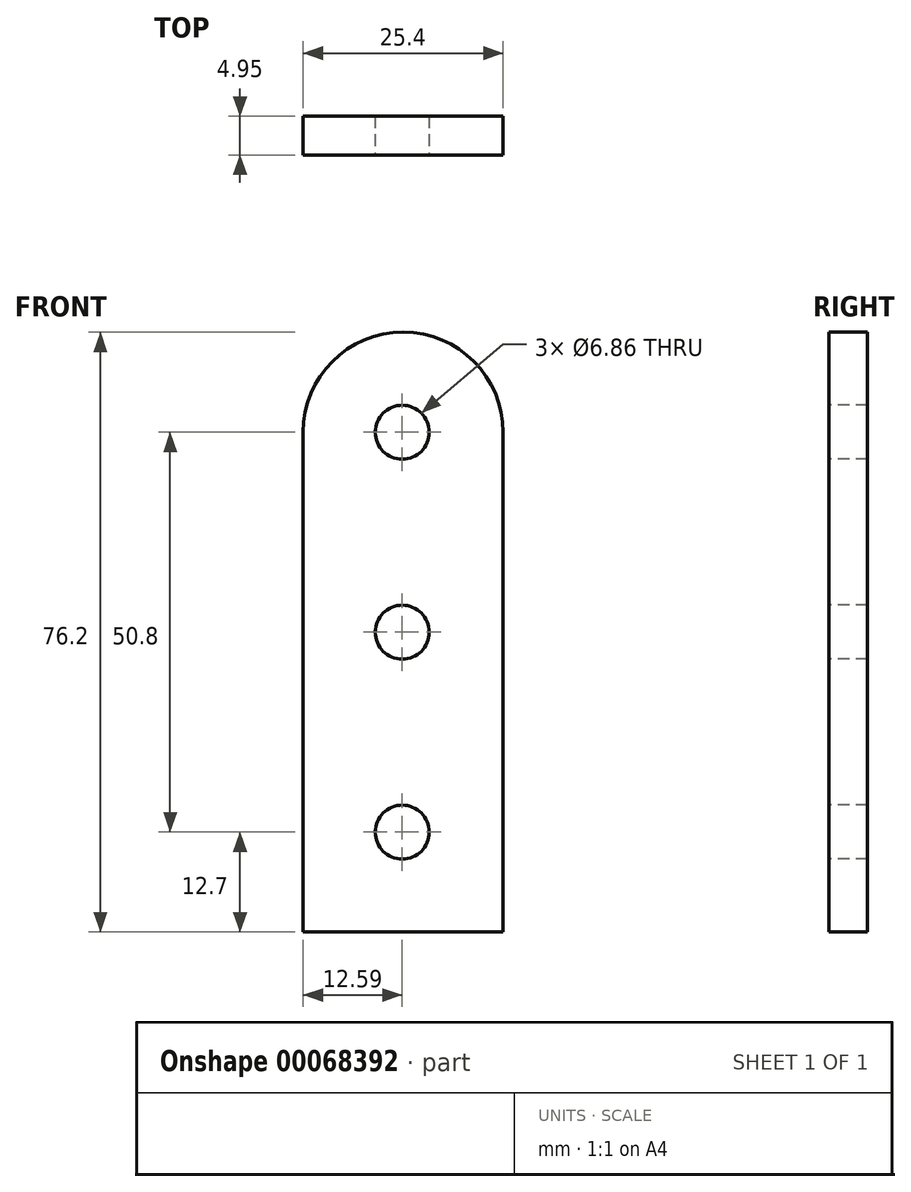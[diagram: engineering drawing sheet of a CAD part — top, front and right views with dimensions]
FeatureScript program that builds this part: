
annotation { "Feature Type Name" : "Feature", "Feature Type Description" : "" }
export const myFeature = defineFeature(function(context is Context, id is Id, definition is map)
    precondition{}
    {
        {
            var Q0;
            Q0=qCreatedBy(makeId("Front.planeOp"),FACE);
            var sketch = newSketch(context, id + "F0", { "sketchPlane" : qUnion([Q0])});
            skLineSegment(sketch, "E0.bottom", {"start": v(12.81, 0) * mm, "end": v(-12.59, 0) * mm});
            skLineSegment(sketch, "E0.top", {"start": v(12.81, 63.5) * mm, "end": v(-12.59, 63.5) * mm});
            skLineSegment(sketch, "E0.left", {"start": v(12.81, 0) * mm, "end": v(12.81, 63.5) * mm});
            skLineSegment(sketch, "E0.right", {"start": v(-12.59, 0) * mm, "end": v(-12.59, 63.5) * mm});
            skCircle(sketch, "E1", {"center": v(0.11, 63.5) * mm, "radius": 12.7 * mm});
            skSolve(sketch);
        }
        {
            var Q0;
            Q0 = qSketchRegion(id + "F0", true);
            extrude(context, id + "F1", {"entities" : qUnion([Q0]), "depth" : 4.95 * mm});
        }
        {
            var Q0;
            Q0=makeQuery(id+"F1.opExtrude","CAP_FACE",FACE,{"disambiguationData":[OSD([sQuery(id+"F0.wireOp",EDGE,"E0.bottom"),sQuery(id+"F0.wireOp",EDGE,"E0.left"),sQuery(id+"F0.wireOp",EDGE,"E0.right"),sQuery(id+"F0.wireOp",EDGE,"E1")])],"isStart":false});
            var sketch = newSketch(context, id + "F2", { "sketchPlane" : qUnion([Q0])});
            skLineSegment(sketch, "E2", {"start": v(0, 0) * mm, "end": v(0, 12.7) * mm, "construction": true});
            skLineSegment(sketch, "E3", {"start": v(0, 12.7) * mm, "end": v(0, 38.1) * mm, "construction": true});
            skLineSegment(sketch, "E4", {"start": v(0, 38.1) * mm, "end": v(0, 63.5) * mm, "construction": true});
            skCircle(sketch, "E5", {"center": v(0, 12.7) * mm, "radius": 3.43 * mm});
            skCircle(sketch, "E6", {"center": v(0, 38.1) * mm, "radius": 3.43 * mm});
            skCircle(sketch, "E7", {"center": v(0, 63.5) * mm, "radius": 3.43 * mm});
            skSolve(sketch);
        }
        {
            var Q0;
            Q0 = qSketchRegion(id + "F2", true);
            extrude(context, id + "F3", {"entities" : qUnion([Q0]), "operationType" : NewBodyOperationType.REMOVE, "oppositeDirection" : true, "depth" : 25.4 * mm});
        }
    });
